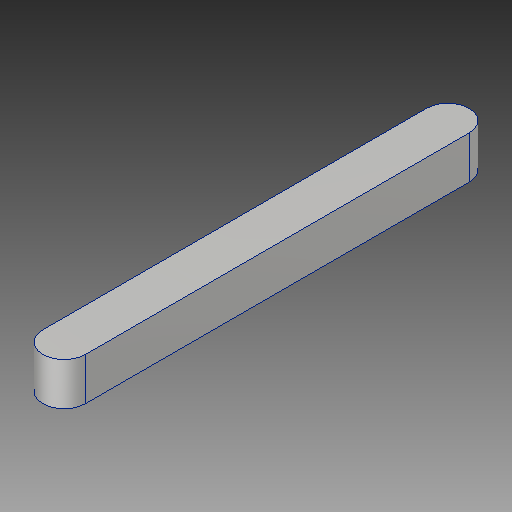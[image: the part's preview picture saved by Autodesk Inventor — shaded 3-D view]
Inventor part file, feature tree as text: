
AUTODESK INVENTOR PART (.ipt)
format: ipt  version: 2017 (Build 210142000, 142)  size: 80,384 bytes
history: native  units: in
note: dims shown in document units (in); Inventor stores cm internally (conversion verified against a paired STEP export)
features: fillet x1
ambient origin geometry x8: Origin, YZ Plane, XZ Plane, XY Plane, X Axis, Y Axis, Z Axis, Center Point
bodies: Solid1 (feature_tree)
feature tree (1):
  fillet  "Fillet1"  [1 undecoded]
note: 1 required parameter value undecoded (feature->parameter linkage not recoverable at this tier; creation-order binding heuristic only, values carry confidence <= 0.55)
